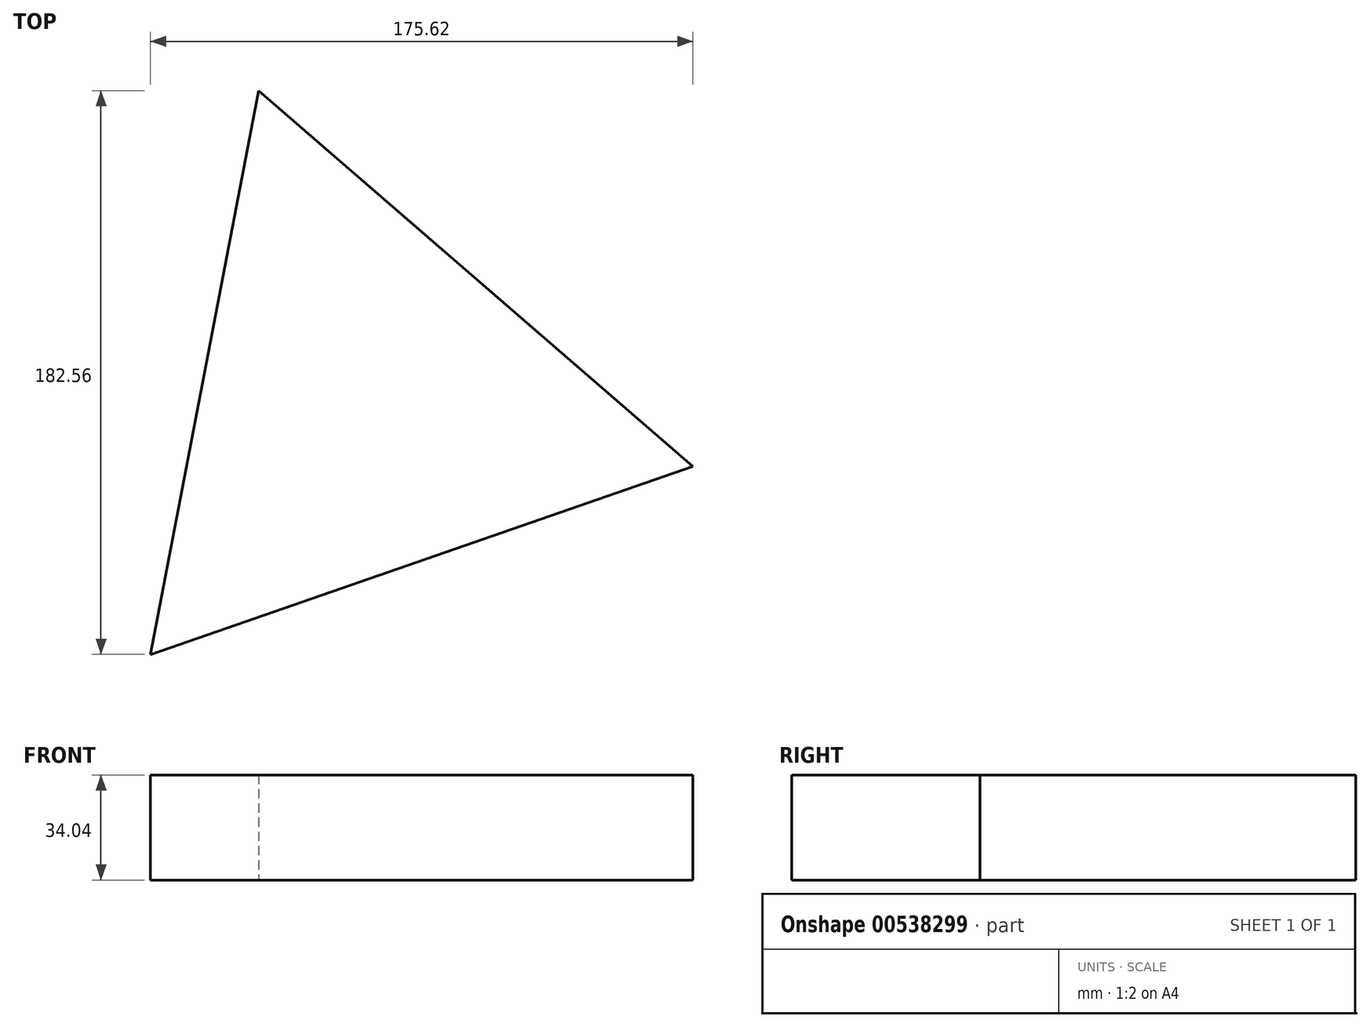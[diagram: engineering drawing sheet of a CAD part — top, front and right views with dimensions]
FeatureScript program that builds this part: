
annotation { "Feature Type Name" : "Feature", "Feature Type Description" : "" }
export const myFeature = defineFeature(function(context is Context, id is Id, definition is map)
    precondition{}
    {
        {
            var Q0;
            Q0=qCreatedBy(makeId("Top.planeOp"),FACE);
            var sketch = newSketch(context, id + "F0", { "sketchPlane" : qUnion([Q0])});
            skCircle(sketch, "E0.cCircle", {"center": v(0, 0) * mm, "radius": 53.66 * mm, "construction": true});
            skLineSegment(sketch, "E0.0", {"start": v(-35.18, 101.4) * mm, "end": v(105.4, -20.24) * mm});
            skLineSegment(sketch, "E0.1", {"start": v(105.4, -20.24) * mm, "end": v(-70.22, -81.16) * mm});
            skLineSegment(sketch, "E0.2", {"start": v(-70.22, -81.16) * mm, "end": v(-35.18, 101.4) * mm});
            skPoint(sketch, "E0.0.midPoint", {"position": v(35.11, 40.58) * mm});
            skSolve(sketch);
        }
        {
            var Q0;
            Q0 = qSketchRegion(id + "F0", true);
            extrude(context, id + "F1", {"entities" : qUnion([Q0]), "depth" : 34.04 * mm, "offsetDistance" : 25.4 * mm});
        }
    });
